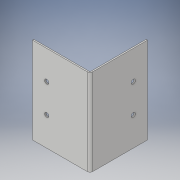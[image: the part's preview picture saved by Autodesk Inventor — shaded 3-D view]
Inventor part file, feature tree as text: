
AUTODESK INVENTOR PART (.ipt)
format: ipt  version: 2019 (Build 230136000, 136)  size: 114,176 bytes
history: native  units: mm
features: extrude x3, sketch x2, fillet x1
ambient origin geometry x8: Origin, YZ Plane, XZ Plane, XY Plane, X Axis, Y Axis, Z Axis, Center Point
bodies: Solid1 (feature_tree)
feature tree (6):
  extrude  "Extrusion1"  Depth=1.0mm
  fillet  "Fillet1"  Radius=60.0mm
  extrude  "Extrusion4"  Depth=40.0mm
  extrude  "Extrusion5"  Depth=1.0mm
  sketch  "Sketch4"  dims[d0=60.0mm d2=1.0mm d4=60.0mm d5=0.0mm]
  sketch  "Sketch5"  dims[d6=2.0mm d15=40.0mm d17=3.0mm d18=3.0mm d19=1.0mm d20=0.0mm d24=40.0mm d25=3.0mm d27=3.0mm d28=1.0mm d29=0.0mm]
